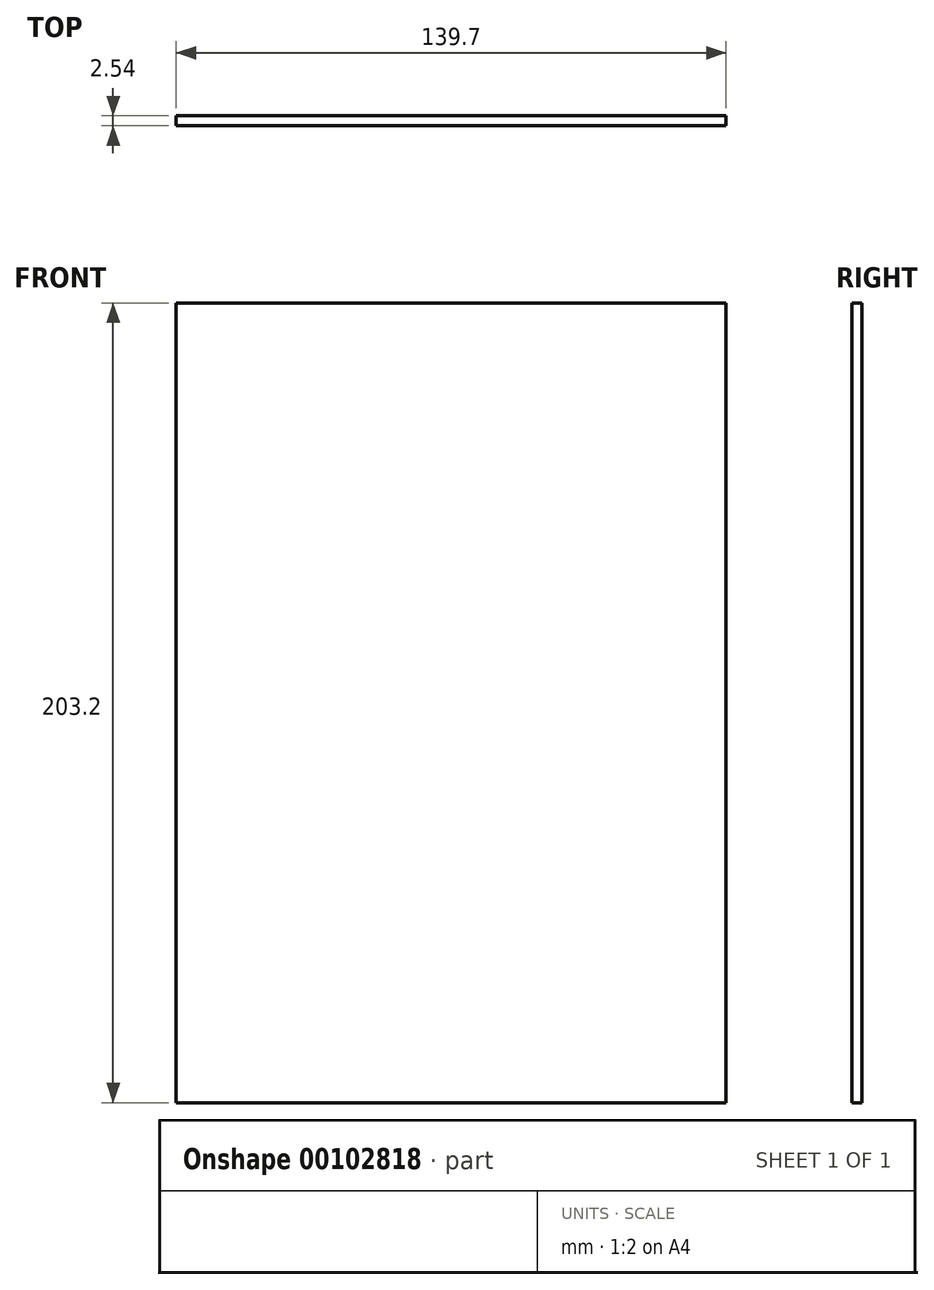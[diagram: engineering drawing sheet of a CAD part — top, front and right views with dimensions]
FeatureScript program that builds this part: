
annotation { "Feature Type Name" : "Feature", "Feature Type Description" : "" }
export const myFeature = defineFeature(function(context is Context, id is Id, definition is map)
    precondition{}
    {
        {
            var Q0;
            Q0=qCreatedBy(makeId("Front.planeOp"),FACE);
            var sketch = newSketch(context, id + "F0", { "sketchPlane" : qUnion([Q0])});
            skLineSegment(sketch, "E0", {"start": v(-63.75, -19.8) * mm, "end": v(75.95, -19.8) * mm});
            skLineSegment(sketch, "E1", {"start": v(75.95, -19.8) * mm, "end": v(75.95, 183.4) * mm});
            skLineSegment(sketch, "E2", {"start": v(75.95, 183.4) * mm, "end": v(-63.75, 183.4) * mm});
            skLineSegment(sketch, "E3", {"start": v(-63.75, 183.4) * mm, "end": v(-63.75, -19.8) * mm});
            skSolve(sketch);
        }
        {
            var Q0;
            Q0=makeQuery(id+"F0.imprint","IMPRINT",FACE,{"disambiguationData":[TD([[makeQuery(id+"F0.imprint","IMPRINT",EDGE,{"derivedFrom":sQuery(id+"F0.wireOp",EDGE,"E0")}),1.0]])]});
            extrude(context, id + "F1", {"entities" : qUnion([Q0]), "oppositeDirection" : true, "depth" : 2.54 * mm});
        }
    });
